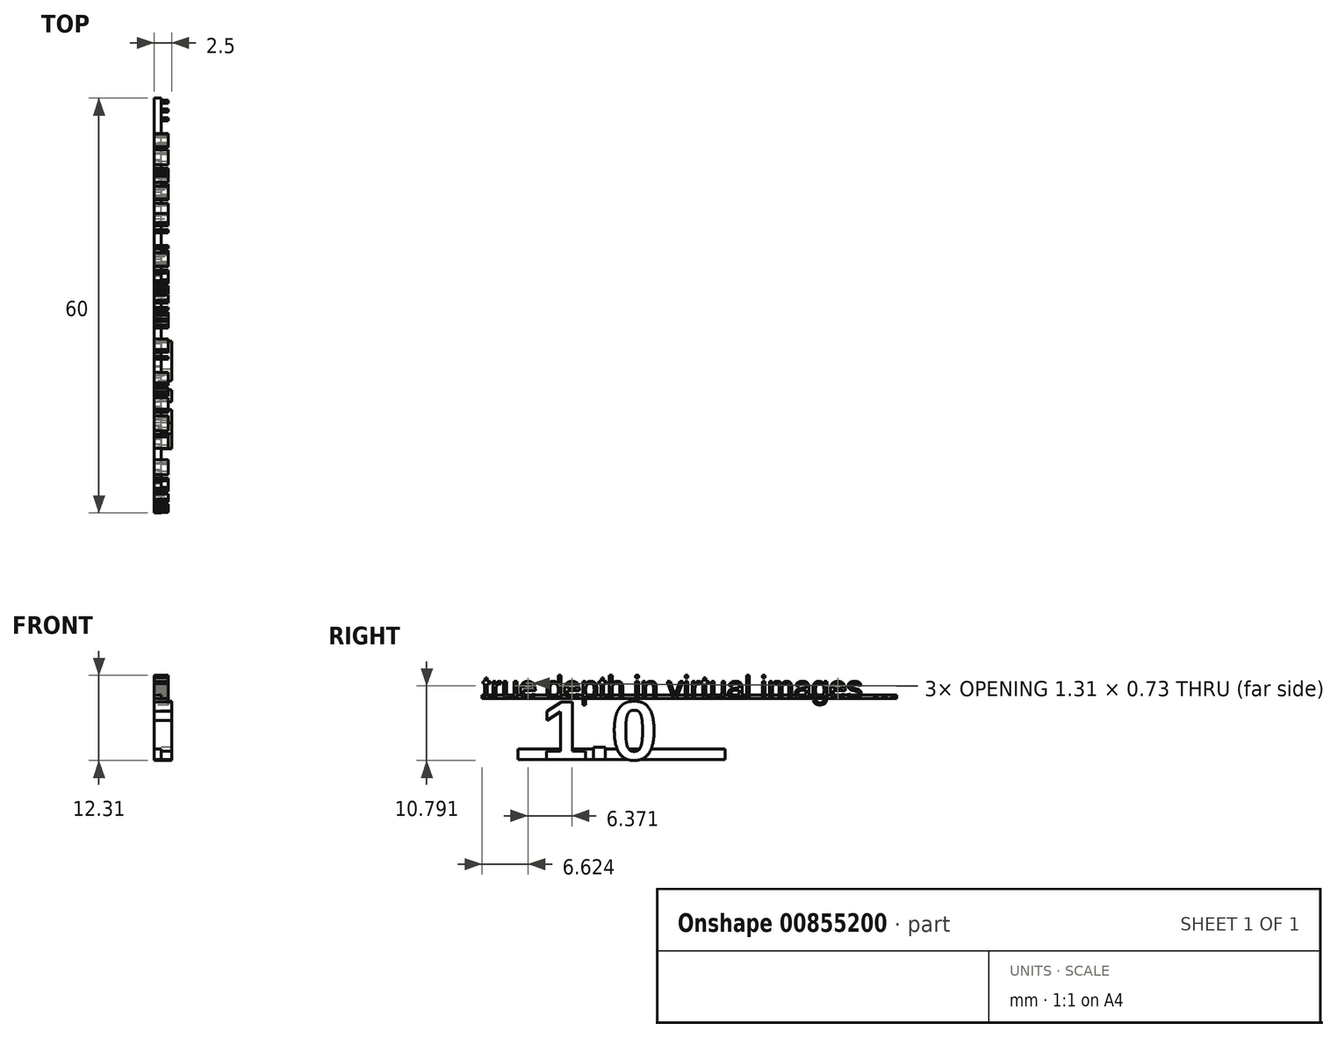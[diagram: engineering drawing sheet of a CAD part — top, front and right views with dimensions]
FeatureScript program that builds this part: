
annotation { "Feature Type Name" : "Feature", "Feature Type Description" : "" }
export const myFeature = defineFeature(function(context is Context, id is Id, definition is map)
    precondition{}
    {
        {
            var Q0;
            Q0=qCreatedBy(makeId("Right.planeOp"),FACE);
            var sketch = newSketch(context, id + "F0", { "sketchPlane" : qUnion([Q0])});
            skText(sketch, "E0", { "text": "true depth in virtual images ...", "fontName": "Arimo-Regular.ttf"});
            const initialGuessF0  = {"E0": [-0.00886, 0.00647, 1, 0, 0.0033]};
            skSetInitialGuess(sketch, initialGuessF0);
            skSolve(sketch);
        }
        {
            var Q0;
            Q0=qCreatedBy(makeId("Right.planeOp"),FACE);
            var sketch = newSketch(context, id + "F1", { "sketchPlane" : qUnion([Q0])});
            skLineSegment(sketch, "E1.0", {"start": v(-8.86, 6.47) * mm, "end": v(-8.86, 9.77) * mm, "construction": true});
            skLineSegment(sketch, "E2.0", {"start": v(51.14, 6.47) * mm, "end": v(51.14, 9.77) * mm, "construction": true});
            skLineSegment(sketch, "E3.0", {"start": v(-8.86, 6.47) * mm, "end": v(51.14, 6.47) * mm, "construction": true});
            skLineSegment(sketch, "E4.bottom", {"start": v(-8.86, 6.97) * mm, "end": v(51.14, 6.97) * mm});
            skLineSegment(sketch, "E4.top", {"start": v(-8.86, 6.47) * mm, "end": v(51.14, 6.47) * mm});
            skLineSegment(sketch, "E4.left", {"start": v(-8.86, 6.97) * mm, "end": v(-8.86, 6.47) * mm});
            skLineSegment(sketch, "E4.right", {"start": v(51.14, 6.97) * mm, "end": v(51.14, 6.47) * mm});
            skSolve(sketch);
        }
        {
            var Q0;
            Q0 = qSketchRegion(id + "F1", true);
            extrude(context, id + "F2", {"entities" : qUnion([Q0]), "depth" : 1 * mm, "offsetDistance" : 25 * mm});
        }
        {
            var Q0;
            Q0 = qSketchRegion(id + "F0", true);
            extrude(context, id + "F3", {"entities" : qUnion([Q0]), "operationType" : NewBodyOperationType.ADD, "depth" : 2 * mm, "offsetDistance" : 25 * mm});
        }
        {
            var Q0;
            Q0=qCreatedBy(makeId("Right.planeOp"),FACE);
            var sketch = newSketch(context, id + "F4", { "sketchPlane" : qUnion([Q0])});
            skText(sketch, "E5", { "text": " 1.0", "fontName": "Arimo-Bold.ttf"});
            const initialGuessF4  = {"E5": [-0.00369, -0.0024, 1, 0, 0.00872]};
            skSetInitialGuess(sketch, initialGuessF4);
            skSolve(sketch);
        }
        {
            var Q0;
            Q0=qCreatedBy(makeId("Right.planeOp"),FACE);
            var sketch = newSketch(context, id + "F5", { "sketchPlane" : qUnion([Q0])});
            skLineSegment(sketch, "E6.0", {"start": v(-3.69, -2.4) * mm, "end": v(-3.69, 6.33) * mm, "construction": true});
            skLineSegment(sketch, "E7.0", {"start": v(-3.69, -2.4) * mm, "end": v(26.31, -2.4) * mm, "construction": true});
            skLineSegment(sketch, "E8.0", {"start": v(26.31, -2.4) * mm, "end": v(26.31, 6.33) * mm, "construction": true});
            skLineSegment(sketch, "E9.bottom", {"start": v(-3.69, -0.9) * mm, "end": v(26.31, -0.9) * mm});
            skLineSegment(sketch, "E9.top", {"start": v(-3.69, -2.4) * mm, "end": v(26.31, -2.4) * mm});
            skLineSegment(sketch, "E9.left", {"start": v(-3.69, -0.9) * mm, "end": v(-3.69, -2.4) * mm});
            skLineSegment(sketch, "E9.right", {"start": v(26.31, -0.9) * mm, "end": v(26.31, -2.4) * mm});
            skSolve(sketch);
        }
        {
            var Q0;
            Q0 = qSketchRegion(id + "F5", true);
            extrude(context, id + "F6", {"entities" : qUnion([Q0]), "depth" : 1 * mm, "offsetDistance" : 25 * mm});
        }
        {
            var Q0;
            Q0 = qSketchRegion(id + "F4", true);
            extrude(context, id + "F7", {"entities" : qUnion([Q0]), "operationType" : NewBodyOperationType.ADD, "depth" : 2.5 * mm, "offsetDistance" : 25 * mm});
        }
    });
